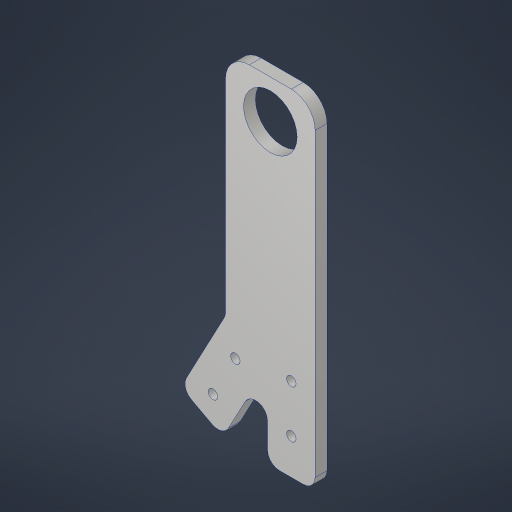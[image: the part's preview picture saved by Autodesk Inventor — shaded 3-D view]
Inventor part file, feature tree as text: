
AUTODESK INVENTOR PART (.ipt)
format: ipt  version: 2023.4 (Build 274418000, 418)  size: 245,248 bytes
history: native  units: in
note: dims shown in document units (in); Inventor stores cm internally (conversion verified against a paired STEP export)
features: projected_geometry x3, sketch x2, extrude x2, hole x2, fillet x2
ambient origin geometry x8: Origin, YZ Plane, XZ Plane, XY Plane, X Axis, Y Axis, Z Axis, Center Point
bodies: Solid1 (feature_tree)
feature tree (11):
  sketch  "Sketch1"  dims[d0=1.0in d1=1.0in]
  extrude  "Extrusion1"  Depth=1.0in
  hole  "Hole1"  [1 undecoded]
  sketch  "Sketch2"  dims[d2=0.1924in d3=2.0in d4=1.0in d5=0.5in d6=1.0in d7=0.5in d8=2.25in d9=0.25in d10=0.0in d11=0.201in d12=0.75in d13=0.385in d14=0.25in d15=0.5635in d16=1.0in d17=0.8108in d18=0.25in d19=1.125in d20=4.0in d22=1.0in d23=0.0in d24=1.125in d25=0.75in d26=0.385in d27=0.25in d28=0.5635in d29=1.0in d30=0.8108in d31=0.5in d32=0.25in d36=0.0in d37=0.25in d38=0.25in]
  extrude  "Extrusion2"  Depth=1.0in
  fillet  "Fillet1"  Radius=0.5in
  hole  "Hole2"  [1 undecoded]
  fillet  "Fillet2"  Radius=0.5in
  projected_geometry  "Projected Loop1"
  projected_geometry  "Project Cut Edges1"
  projected_geometry  "Project Cut Edges2"
note: 2 required parameter values undecoded (feature->parameter linkage not recoverable at this tier; creation-order binding heuristic only, values carry confidence <= 0.55)
